# Revit family: Wall_Mount-Sliding-Phantom_Screens-Single_Parting-Manual_Wall_Screen-CS
name_source: partatom
category: Specialty Equipment
revit_build: Autodesk Revit 2017 (Build: 20160225_1515(x64)
units: mm (PartAtom-declared; Revit-internal decimal feet)

## family parameters
Always vertical = Yes
Cut with Voids When Loaded = No
OmniClass Number = 23.30.60.21
OmniClass Title = Insect Screens
Part Type = Normal
Room Calculation Point = No
Round Connector Dimension = Use Diameter
Shared = No
Work Plane-Based = No

## types (1)
- Latch Handle
    Assembly Code = B2010300
    Bottom Latch Offset = 0' - 1 1/4"
    Bottom Track = Yes
    Description = Phantom oversized retractable door screen
    Door Bottom Offset = 0' - 1 5/32"
    Finish = Metal-Aluminum-Phantom_Screens-Classic_White
    Finish Screen = Screen-Insect_Mesh-Phantom_Screens-BetterVue_Mesh
    Latch Handle = Yes
    Manufacturer = Phantom Mfg. (Int'l) Ltd.
    Max Height = 10' - 0"
    Max Width = 12' - 0"
    Model = Latch and Release System
    Product Documentation Link = https://www.phantomscreens.com
    Product Name = Manual Wall Screens
    Product Page URL = https://www.phantomscreens.com
    Recessed Cup Height = 0' - 0 1/8"
    Recessed Track = No
    Side Housing Offset = 0' - 0"
    Thickness = 0' - 1 23/32"
    Type Comments = Single Parting Screen
    URL = https://www.phantomscreens.com

## geometry (parser evidence)
native form markers: Extrusion x12, Sweep x20
no freeform markers — native parametric forms only
